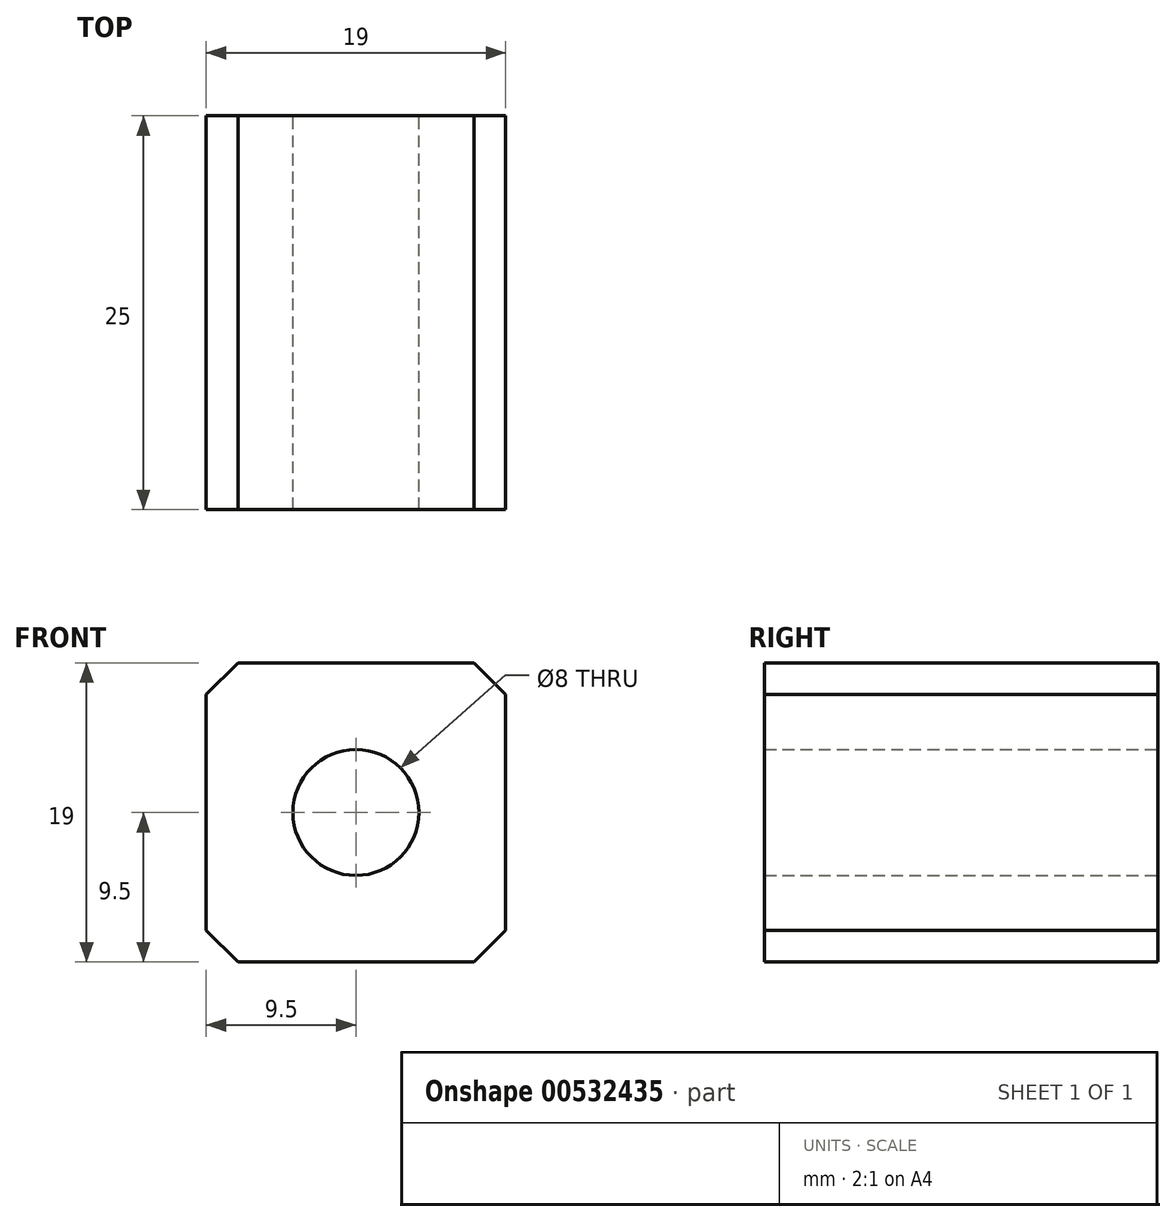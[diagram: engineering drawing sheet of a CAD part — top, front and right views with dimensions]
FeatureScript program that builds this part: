
annotation { "Feature Type Name" : "Feature", "Feature Type Description" : "" }
export const myFeature = defineFeature(function(context is Context, id is Id, definition is map)
    precondition{}
    {
        {
            var Q0;
            Q0=qCreatedBy(makeId("Front.planeOp"),FACE);
            var sketch = newSketch(context, id + "F0", { "sketchPlane" : qUnion([Q0])});
            skLineSegment(sketch, "E0.bottom", {"start": v(9.5, 9.5) * mm, "end": v(-9.5, 9.5) * mm});
            skLineSegment(sketch, "E0.top", {"start": v(9.5, -9.5) * mm, "end": v(-9.5, -9.5) * mm});
            skLineSegment(sketch, "E0.left", {"start": v(9.5, 9.5) * mm, "end": v(9.5, -9.5) * mm});
            skLineSegment(sketch, "E0.right", {"start": v(-9.5, 9.5) * mm, "end": v(-9.5, -9.5) * mm});
            skPoint(sketch, "E0.middle", {"position": v(0, 0) * mm});
            skSolve(sketch);
        }
        {
            var Q0;
            Q0 = qSketchRegion(id + "F0", true);
            extrude(context, id + "F1", {"entities" : qUnion([Q0]), "depth" : 25 * mm, "offsetDistance" : 25 * mm});
        }
        {
            var Q0;
            Q0=makeQuery(id+"F1.opExtrude","CAP_FACE",FACE,{"disambiguationData":[OSD([sQuery(id+"F0.wireOp",EDGE,"E0.bottom"),sQuery(id+"F0.wireOp",EDGE,"E0.top"),sQuery(id+"F0.wireOp",EDGE,"E0.left"),sQuery(id+"F0.wireOp",EDGE,"E0.right")])],"isStart":true});
            var sketch = newSketch(context, id + "F2", { "sketchPlane" : qUnion([Q0])});
            skCircle(sketch, "E1", {"center": v(0, 0) * mm, "radius": 4 * mm});
            skCircle(sketch, "E2", {"center": v(0, 0) * mm, "radius": 9.28 * mm});
            skSolve(sketch);
        }
        {
            var Q0;
            Q0=makeQuery(id+"F1.opExtrude","SWEPT_EDGE",EDGE,{"disambiguationData":[OSD([sQuery(id+"F0.wireOp",EDGE,"E0.top"),sQuery(id+"F0.wireOp",EDGE,"E0.left")])]});
            var Q1;
            Q1=makeQuery(id+"F1.opExtrude","SWEPT_EDGE",EDGE,{"disambiguationData":[OSD([sQuery(id+"F0.wireOp",EDGE,"E0.bottom"),sQuery(id+"F0.wireOp",EDGE,"E0.left")])]});
            chamfer(context, id + "F3", {"entities" : qUnion([Q0, Q1]), "width" : 2 * mm, "tangentPropagation" : true});
        }
        {
            var Q0;
            Q0=makeQuery(id+"F1.opExtrude","SWEPT_EDGE",EDGE,{"disambiguationData":[OSD([sQuery(id+"F0.wireOp",EDGE,"E0.bottom"),sQuery(id+"F0.wireOp",EDGE,"E0.right")])]});
            chamfer(context, id + "F4", {"entities" : qUnion([Q0]), "width" : 2 * mm, "tangentPropagation" : true});
        }
        {
            var Q0;
            Q0=makeQuery(id+"F1.opExtrude","SWEPT_EDGE",EDGE,{"disambiguationData":[OSD([sQuery(id+"F0.wireOp",EDGE,"E0.top"),sQuery(id+"F0.wireOp",EDGE,"E0.right")])]});
            chamfer(context, id + "F5", {"entities" : qUnion([Q0]), "width" : 2 * mm, "tangentPropagation" : true});
        }
        {
            var Q0;
            Q0=makeQuery(id+"F2.imprint","IMPRINT",FACE,{"disambiguationData":[TD([[makeQuery(id+"F2.imprint","IMPRINT",EDGE,{"derivedFrom":sQuery(id+"F2.wireOp",EDGE,"E1")}),1.0]])]});
            extrude(context, id + "F6", {"entities" : qUnion([Q0]), "operationType" : NewBodyOperationType.REMOVE, "oppositeDirection" : true, "depth" : 25 * mm, "offsetDistance" : 25 * mm});
        }
    });
